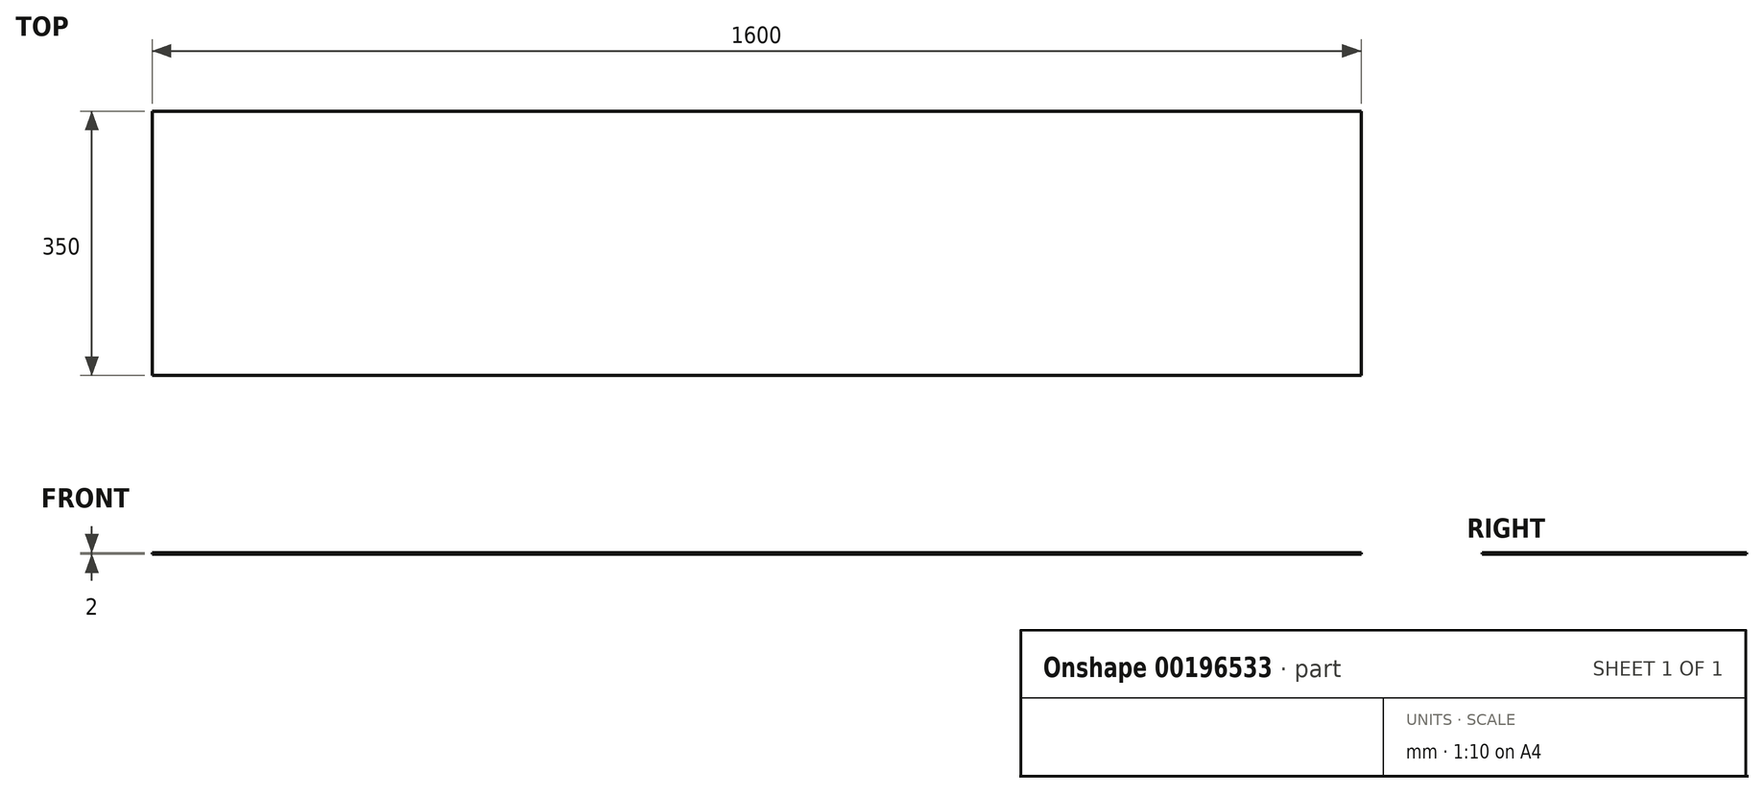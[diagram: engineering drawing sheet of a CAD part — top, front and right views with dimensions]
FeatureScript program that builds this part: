
annotation { "Feature Type Name" : "Feature", "Feature Type Description" : "" }
export const myFeature = defineFeature(function(context is Context, id is Id, definition is map)
    precondition{}
    {
        {
            var Q0;
            Q0=qCreatedBy(makeId("Top.planeOp"),FACE);
            var sketch = newSketch(context, id + "F0", { "sketchPlane" : qUnion([Q0])});
            skLineSegment(sketch, "E0.bottom", {"start": v(-864.34, -235.28) * mm, "end": v(735.66, -235.28) * mm});
            skLineSegment(sketch, "E0.top", {"start": v(-864.34, 114.72) * mm, "end": v(735.66, 114.72) * mm});
            skLineSegment(sketch, "E0.left", {"start": v(-864.34, -235.28) * mm, "end": v(-864.34, 114.72) * mm});
            skLineSegment(sketch, "E0.right", {"start": v(735.66, -235.28) * mm, "end": v(735.66, 114.72) * mm});
            skSolve(sketch);
        }
        {
            var Q0;
            Q0=makeQuery(id+"F0.imprint","IMPRINT",FACE,{"disambiguationData":[TD([[makeQuery(id+"F0.imprint","IMPRINT",EDGE,{"derivedFrom":sQuery(id+"F0.wireOp",EDGE,"E0.bottom")}),1.0]])]});
            extrude(context, id + "F1", {"entities" : qUnion([Q0]), "depth" : 2 * mm});
        }
    });
